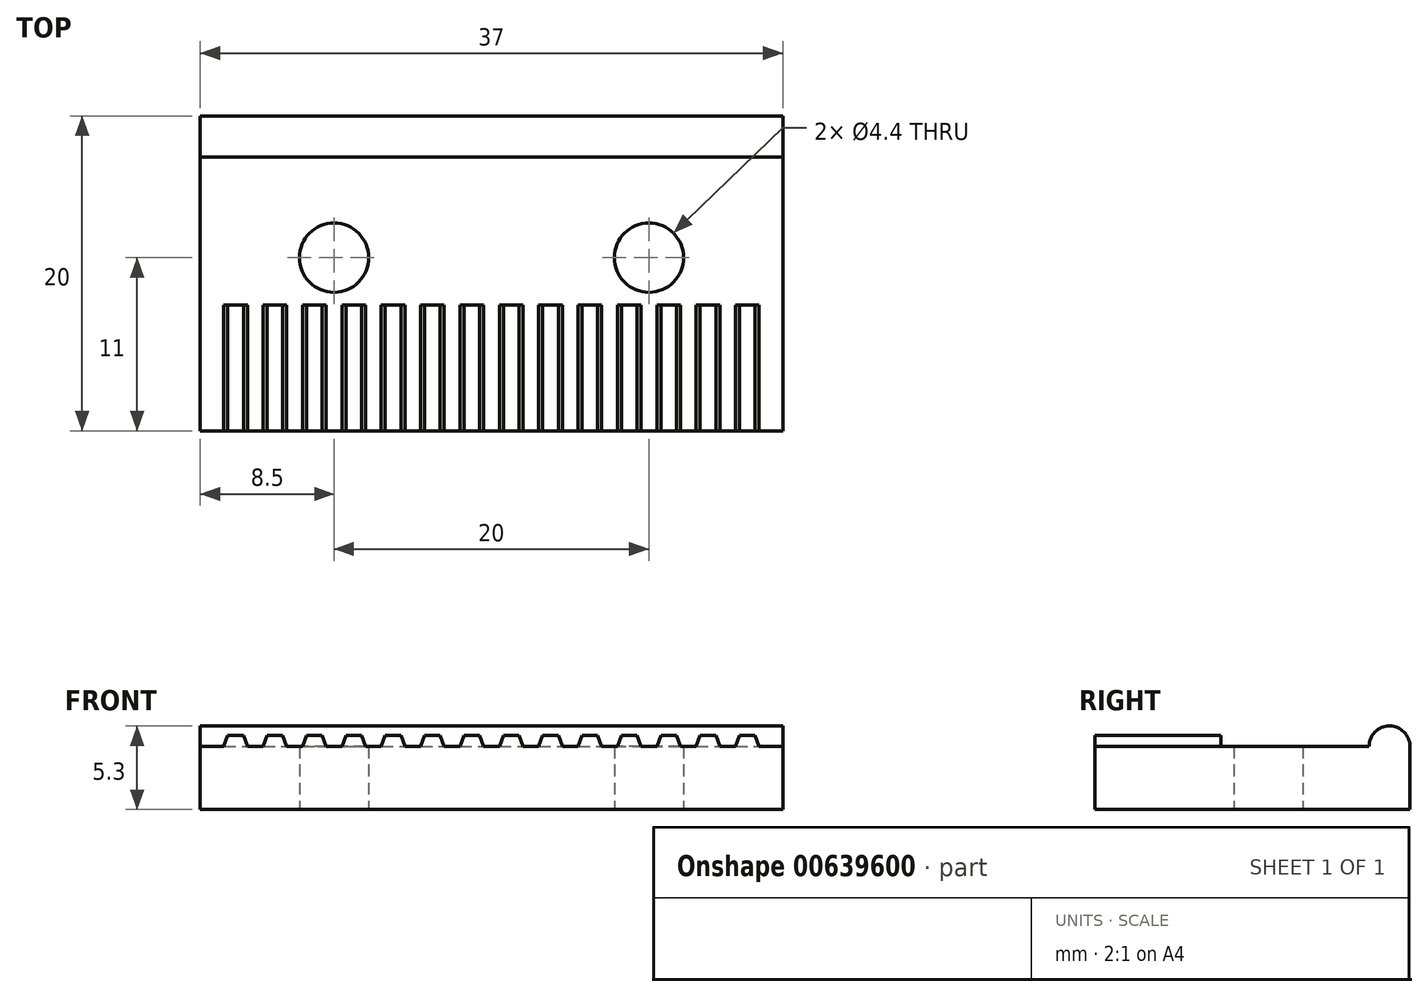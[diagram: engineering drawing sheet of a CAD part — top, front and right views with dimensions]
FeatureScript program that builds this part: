
annotation { "Feature Type Name" : "Feature", "Feature Type Description" : "" }
export const myFeature = defineFeature(function(context is Context, id is Id, definition is map)
    precondition{}
    {
        {
            var Q0;
            Q0=qCreatedBy(makeId("Front.planeOp"),FACE);
            var sketch = newSketch(context, id + "F0", { "sketchPlane" : qUnion([Q0])});
            skLineSegment(sketch, "E0.bottom", {"start": v(18.5, 0) * mm, "end": v(-18.5, 0) * mm});
            skLineSegment(sketch, "E0.top", {"start": v(18.5, 4) * mm, "end": v(-18.5, 4) * mm});
            skLineSegment(sketch, "E0.left", {"start": v(18.5, 0) * mm, "end": v(18.5, 4) * mm});
            skLineSegment(sketch, "E0.right", {"start": v(-18.5, 0) * mm, "end": v(-18.5, 4) * mm});
            skPoint(sketch, "E0.middle", {"position": v(0, 2) * mm});
            skSolve(sketch);
        }
        {
            var Q0;
            Q0 = qSketchRegion(id + "F0", true);
            extrude(context, id + "F1", {"entities" : qUnion([Q0]), "depth" : 20 * mm, "offsetDistance" : 25 * mm});
        }
        {
            var Q0;
            Q0=makeQuery(id+"F1.opExtrude","CAP_FACE",FACE,{"disambiguationData":[OSD([sQuery(id+"F0.wireOp",EDGE,"E0.bottom"),sQuery(id+"F0.wireOp",EDGE,"E0.top"),sQuery(id+"F0.wireOp",EDGE,"E0.left"),sQuery(id+"F0.wireOp",EDGE,"E0.right")])],"isStart":false});
            var sketch = newSketch(context, id + "F2", { "sketchPlane" : qUnion([Q0])});
            skLineSegment(sketch, "E1", {"start": v(0.5, 4) * mm, "end": v(0.75, 4.7) * mm});
            skLineSegment(sketch, "E2", {"start": v(0.75, 4.7) * mm, "end": v(1.75, 4.7) * mm});
            skLineSegment(sketch, "E3", {"start": v(1.75, 4.7) * mm, "end": v(2, 4) * mm});
            skLineSegment(sketch, "E4", {"start": v(2, 4) * mm, "end": v(0.5, 4) * mm});
            skLineSegment(sketch, "E5.MirrorCS", {"start": v(-0.5, 4) * mm, "end": v(-0.75, 4.7) * mm});
            skLineSegment(sketch, "E6.MirrorCS", {"start": v(-0.75, 4.7) * mm, "end": v(-1.75, 4.7) * mm});
            skLineSegment(sketch, "E7.MirrorCS", {"start": v(-2, 4) * mm, "end": v(-0.5, 4) * mm});
            skLineSegment(sketch, "E8.MirrorCS", {"start": v(-1.75, 4.7) * mm, "end": v(-2, 4) * mm});
            skPoint(sketch, "E9", {"position": v(1.25, 4.7) * mm});
            skPoint(sketch, "E10", {"position": v(-1.25, 4.7) * mm});
            skLineSegment(sketch, "E11.1.0.0", {"start": v(4.25, 4.7) * mm, "end": v(4.5, 4) * mm});
            skLineSegment(sketch, "E11.1.0.1", {"start": v(4.5, 4) * mm, "end": v(3, 4) * mm});
            skLineSegment(sketch, "E11.1.0.2", {"start": v(3.25, 4.7) * mm, "end": v(4.25, 4.7) * mm});
            skLineSegment(sketch, "E11.1.0.3", {"start": v(3, 4) * mm, "end": v(3.25, 4.7) * mm});
            skPoint(sketch, "E11.1.0.4", {"position": v(3.75, 4.7) * mm});
            skLineSegment(sketch, "E11.2.0.0", {"start": v(6.75, 4.7) * mm, "end": v(7, 4) * mm});
            skLineSegment(sketch, "E11.2.0.1", {"start": v(7, 4) * mm, "end": v(5.5, 4) * mm});
            skLineSegment(sketch, "E11.2.0.2", {"start": v(5.75, 4.7) * mm, "end": v(6.75, 4.7) * mm});
            skLineSegment(sketch, "E11.2.0.3", {"start": v(5.5, 4) * mm, "end": v(5.75, 4.7) * mm});
            skPoint(sketch, "E11.2.0.4", {"position": v(6.25, 4.7) * mm});
            skLineSegment(sketch, "E11.3.0.0", {"start": v(9.25, 4.7) * mm, "end": v(9.5, 4) * mm});
            skLineSegment(sketch, "E11.3.0.1", {"start": v(9.5, 4) * mm, "end": v(8, 4) * mm});
            skLineSegment(sketch, "E11.3.0.2", {"start": v(8.25, 4.7) * mm, "end": v(9.25, 4.7) * mm});
            skLineSegment(sketch, "E11.3.0.3", {"start": v(8, 4) * mm, "end": v(8.25, 4.7) * mm});
            skPoint(sketch, "E11.3.0.4", {"position": v(8.75, 4.7) * mm});
            skLineSegment(sketch, "E11.4.0.0", {"start": v(11.75, 4.7) * mm, "end": v(12, 4) * mm});
            skLineSegment(sketch, "E11.4.0.1", {"start": v(12, 4) * mm, "end": v(10.5, 4) * mm});
            skLineSegment(sketch, "E11.4.0.2", {"start": v(10.75, 4.7) * mm, "end": v(11.75, 4.7) * mm});
            skLineSegment(sketch, "E11.4.0.3", {"start": v(10.5, 4) * mm, "end": v(10.75, 4.7) * mm});
            skPoint(sketch, "E11.4.0.4", {"position": v(11.25, 4.7) * mm});
            skLineSegment(sketch, "E11.5.0.0", {"start": v(14.25, 4.7) * mm, "end": v(14.5, 4) * mm});
            skLineSegment(sketch, "E11.5.0.1", {"start": v(14.5, 4) * mm, "end": v(13, 4) * mm});
            skLineSegment(sketch, "E11.5.0.2", {"start": v(13.25, 4.7) * mm, "end": v(14.25, 4.7) * mm});
            skLineSegment(sketch, "E11.5.0.3", {"start": v(13, 4) * mm, "end": v(13.25, 4.7) * mm});
            skPoint(sketch, "E11.5.0.4", {"position": v(13.75, 4.7) * mm});
            skLineSegment(sketch, "E11.6.0.0", {"start": v(16.75, 4.7) * mm, "end": v(17, 4) * mm});
            skLineSegment(sketch, "E11.6.0.1", {"start": v(17, 4) * mm, "end": v(15.5, 4) * mm});
            skLineSegment(sketch, "E11.6.0.2", {"start": v(15.75, 4.7) * mm, "end": v(16.75, 4.7) * mm});
            skLineSegment(sketch, "E11.6.0.3", {"start": v(15.5, 4) * mm, "end": v(15.75, 4.7) * mm});
            skPoint(sketch, "E11.6.0.4", {"position": v(16.25, 4.7) * mm});
            skLineSegment(sketch, "E11.direction1", {"start": v(0.5, 4) * mm, "end": v(3, 4) * mm, "construction": true});
            skLineSegment(sketch, "E12.MirrorCS", {"start": v(-8, 4) * mm, "end": v(-8.25, 4.7) * mm});
            skLineSegment(sketch, "E13.MirrorCS", {"start": v(-15.5, 4) * mm, "end": v(-15.75, 4.7) * mm});
            skLineSegment(sketch, "E14.MirrorCS", {"start": v(-6.75, 4.7) * mm, "end": v(-7, 4) * mm});
            skLineSegment(sketch, "E15.MirrorCS", {"start": v(-3, 4) * mm, "end": v(-3.25, 4.7) * mm});
            skLineSegment(sketch, "E16.MirrorCS", {"start": v(-4.25, 4.7) * mm, "end": v(-4.5, 4) * mm});
            skLineSegment(sketch, "E17.MirrorCS", {"start": v(-5.5, 4) * mm, "end": v(-5.75, 4.7) * mm});
            skLineSegment(sketch, "E18.MirrorCS", {"start": v(-9.25, 4.7) * mm, "end": v(-9.5, 4) * mm});
            skLineSegment(sketch, "E19.MirrorCS", {"start": v(-13, 4) * mm, "end": v(-13.25, 4.7) * mm});
            skLineSegment(sketch, "E20.MirrorCS", {"start": v(-14.25, 4.7) * mm, "end": v(-14.5, 4) * mm});
            skLineSegment(sketch, "E21.MirrorCS", {"start": v(-11.75, 4.7) * mm, "end": v(-12, 4) * mm});
            skLineSegment(sketch, "E22.MirrorCS", {"start": v(-10.5, 4) * mm, "end": v(-10.75, 4.7) * mm});
            skLineSegment(sketch, "E23.MirrorCS", {"start": v(-16.75, 4.7) * mm, "end": v(-17, 4) * mm});
            skLineSegment(sketch, "E24.MirrorCS", {"start": v(-13.25, 4.7) * mm, "end": v(-14.25, 4.7) * mm});
            skLineSegment(sketch, "E25.MirrorCS", {"start": v(-8.25, 4.7) * mm, "end": v(-9.25, 4.7) * mm});
            skLineSegment(sketch, "E26.MirrorCS", {"start": v(-10.75, 4.7) * mm, "end": v(-11.75, 4.7) * mm});
            skLineSegment(sketch, "E27.MirrorCS", {"start": v(-3.25, 4.7) * mm, "end": v(-4.25, 4.7) * mm});
            skLineSegment(sketch, "E28.MirrorCS", {"start": v(-5.75, 4.7) * mm, "end": v(-6.75, 4.7) * mm});
            skLineSegment(sketch, "E29.MirrorCS", {"start": v(-15.75, 4.7) * mm, "end": v(-16.75, 4.7) * mm});
            skPoint(sketch, "E30.MirrorP", {"position": v(-3.75, 4.7) * mm});
            skPoint(sketch, "E31.MirrorP", {"position": v(-16.25, 4.7) * mm});
            skLineSegment(sketch, "E32.MirrorCS", {"start": v(-14.5, 4) * mm, "end": v(-13, 4) * mm});
            skLineSegment(sketch, "E33.MirrorCS", {"start": v(-4.5, 4) * mm, "end": v(-3, 4) * mm});
            skLineSegment(sketch, "E34.MirrorCS", {"start": v(-7, 4) * mm, "end": v(-5.5, 4) * mm});
            skPoint(sketch, "E35.MirrorP", {"position": v(-8.75, 4.7) * mm});
            skPoint(sketch, "E36.MirrorP", {"position": v(-13.75, 4.7) * mm});
            skLineSegment(sketch, "E37.MirrorCS", {"start": v(-9.5, 4) * mm, "end": v(-8, 4) * mm});
            skLineSegment(sketch, "E38.MirrorCS", {"start": v(-12, 4) * mm, "end": v(-10.5, 4) * mm});
            skPoint(sketch, "E39.MirrorP", {"position": v(-6.25, 4.7) * mm});
            skPoint(sketch, "E40.MirrorP", {"position": v(-11.25, 4.7) * mm});
            skLineSegment(sketch, "E41.MirrorCS", {"start": v(-17, 4) * mm, "end": v(-15.5, 4) * mm});
            skSolve(sketch);
        }
        {
            var Q0;
            Q0 = qSketchRegion(id + "F2", true);
            extrude(context, id + "F3", {"entities" : qUnion([Q0]), "operationType" : NewBodyOperationType.ADD, "oppositeDirection" : true, "depth" : 8 * mm, "offsetDistance" : 25 * mm});
        }
        {
            var Q0;
            Q0=makeQuery(id+"F1.opExtrude","SWEPT_FACE",FACE,{"disambiguationData":[OSD([sQuery(id+"F0.wireOp",EDGE,"E0.left")])]});
            var sketch = newSketch(context, id + "F4", { "sketchPlane" : qUnion([Q0])});
            skLineSegment(sketch, "E42", {"start": v(0, 4) * mm, "end": v(-2.6, 4) * mm});
            skArc(sketch, "E43", {"start": v(0, 4) * mm, "mid": v(-1.3, 5.3) * mm, "end": v(-2.6, 4) * mm});
            skSolve(sketch);
        }
        {
            var Q0;
            Q0 = qSketchRegion(id + "F4", true);
            var Q1;
            Q1=makeQuery(id+"F1.opExtrude","SWEPT_FACE",FACE,{"disambiguationData":[OSD([sQuery(id+"F0.wireOp",EDGE,"E0.right")])]});
            extrude(context, id + "F5", {"entities" : qUnion([Q0]), "operationType" : NewBodyOperationType.ADD, "endBound" : BoundingType.UP_TO_SURFACE, "oppositeDirection" : true, "depth" : 25 * mm, "endBoundEntityFace" : qUnion([Q1]), "offsetDistance" : 25 * mm});
        }
        {
            var Q0;
            Q0=makeQuery(id+"F1.opExtrude","SWEPT_FACE",FACE,{"disambiguationData":[OSD([sQuery(id+"F0.wireOp",EDGE,"E0.bottom")])]});
            var sketch = newSketch(context, id + "F6", { "sketchPlane" : qUnion([Q0])});
            skPoint(sketch, "E44", {"position": v(10, 9) * mm});
            skPoint(sketch, "E45.MirrorP", {"position": v(-10, 9) * mm});
            skSolve(sketch);
        }
        {
            var Q0;
            Q0=sQuery(id+"F6.wireOp",VERTEX,"E44");
            var Q1;
            Q1=sQuery(id+"F6.wireOp",VERTEX,"E45.MirrorP");
            var Q2;
            Q2=makeQuery(id+"F1.opExtrude","SWEPT_BODY",BODY,{"disambiguationData":[OSD([sQuery(id+"F0.wireOp",EDGE,"E0.bottom"),sQuery(id+"F0.wireOp",EDGE,"E0.top"),sQuery(id+"F0.wireOp",EDGE,"E0.left"),sQuery(id+"F0.wireOp",EDGE,"E0.right")])]});
            hole(context, id + "F7", {"style" : HoleStyle.SIMPLE, "endStyle" : HoleEndStyle.BLIND, "standardTappedOrClearance" : lookupTablePath({ "standard" : "ISO", "fit" : "Normal", "size" : "M4", "type" : "Clearance" }), "standardBlindInLast" : lookupTablePath({ "fit" : "Standard", "standard" : "ISO", "size" : "M4", "type" : "Clearance" }), "holeDiameter" : 4.4 * mm, "majorDiameter" : 5 * mm, "holeDepth" : 10 * mm, "isTappedThrough" : true, "tappedDepth" : 12 * mm, "tapClearance" : 3, "locations" : qUnion([Q0, Q1]), "scope" : qUnion([Q2])});
        }
    });
